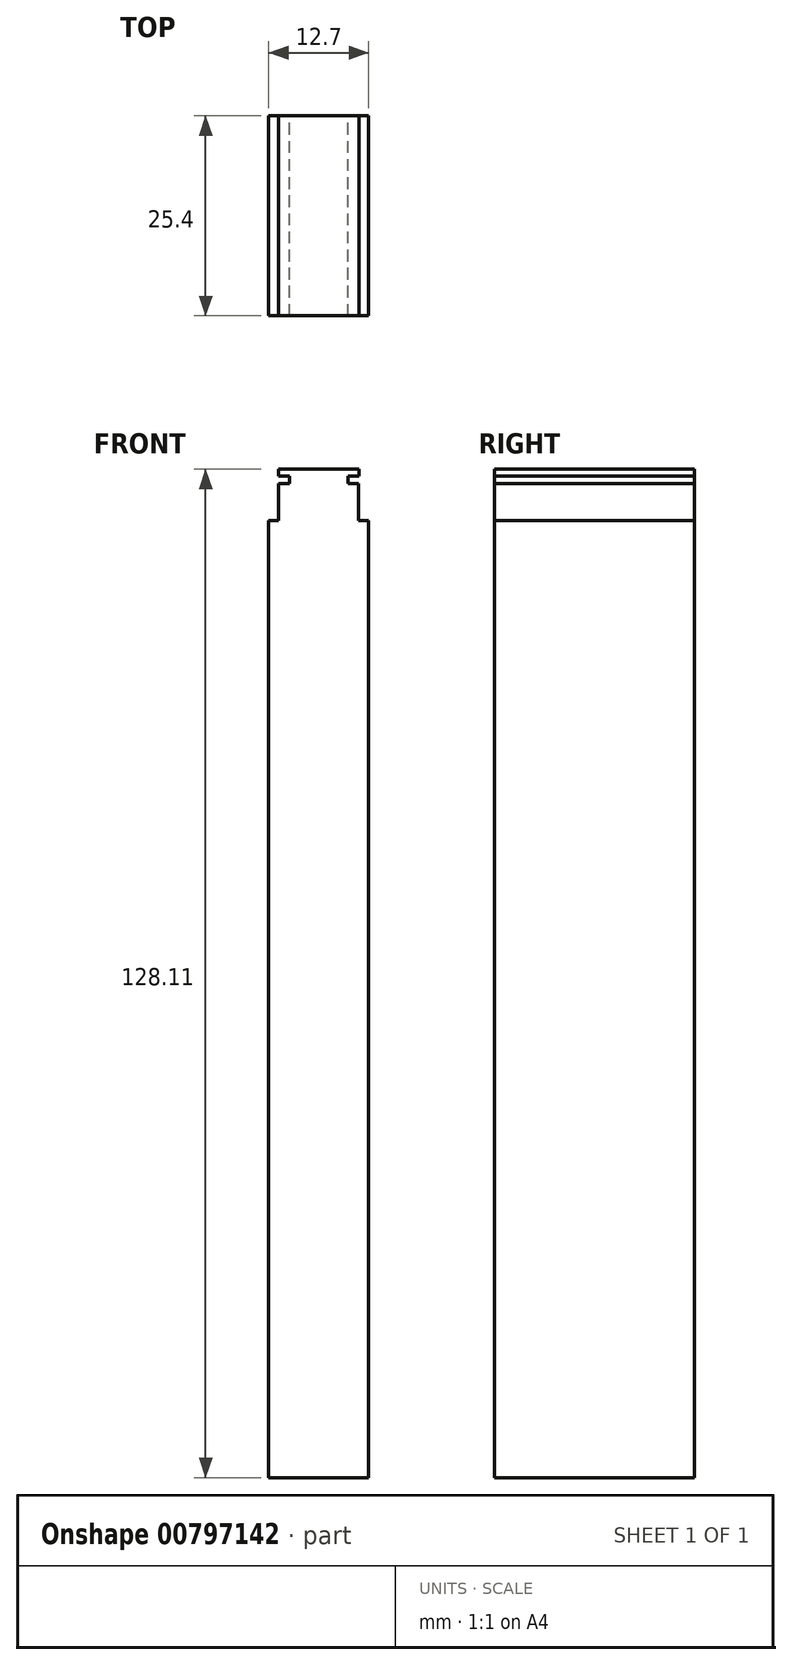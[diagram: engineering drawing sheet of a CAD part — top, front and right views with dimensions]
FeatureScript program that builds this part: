
annotation { "Feature Type Name" : "Feature", "Feature Type Description" : "" }
export const myFeature = defineFeature(function(context is Context, id is Id, definition is map)
    precondition{}
    {
        {
            var Q0;
            Q0=qCreatedBy(makeId("Front.planeOp"),FACE);
            var sketch = newSketch(context, id + "F0", { "sketchPlane" : qUnion([Q0])});
            skLineSegment(sketch, "E0.bottom", {"start": v(-6.35, 60.8) * mm, "end": v(6.35, 60.8) * mm});
            skLineSegment(sketch, "E0.top", {"start": v(-6.35, -60.8) * mm, "end": v(6.35, -60.8) * mm});
            skLineSegment(sketch, "E0.left", {"start": v(-6.35, 60.8) * mm, "end": v(-6.35, -60.8) * mm});
            skLineSegment(sketch, "E0.right", {"start": v(6.35, 60.8) * mm, "end": v(6.35, -60.8) * mm});
            skPoint(sketch, "E0.middle", {"position": v(0, 0) * mm});
            skLineSegment(sketch, "E1", {"start": v(0, 60.8) * mm, "end": v(0, -60.8) * mm});
            skLineSegment(sketch, "E2.bottom", {"start": v(-5.08, 60.8) * mm, "end": v(5.08, 60.8) * mm});
            skLineSegment(sketch, "E2.top", {"start": v(-5.08, 65.5) * mm, "end": v(5.08, 65.5) * mm});
            skLineSegment(sketch, "E2.left", {"start": v(-5.08, 60.8) * mm, "end": v(-5.08, 65.5) * mm});
            skLineSegment(sketch, "E2.right", {"start": v(5.08, 60.8) * mm, "end": v(5.08, 65.5) * mm});
            skLineSegment(sketch, "E3.bottom", {"start": v(-3.69, 65.5) * mm, "end": v(3.69, 65.5) * mm});
            skLineSegment(sketch, "E3.top", {"start": v(-3.69, 66.45) * mm, "end": v(3.69, 66.45) * mm});
            skLineSegment(sketch, "E3.left", {"start": v(-3.69, 65.5) * mm, "end": v(-3.69, 66.45) * mm});
            skLineSegment(sketch, "E3.right", {"start": v(3.69, 65.5) * mm, "end": v(3.69, 66.45) * mm});
            skLineSegment(sketch, "E4.bottom", {"start": v(-5.08, 66.45) * mm, "end": v(5.1, 66.45) * mm});
            skLineSegment(sketch, "E4.top", {"start": v(-5.08, 67.3) * mm, "end": v(5.1, 67.3) * mm});
            skLineSegment(sketch, "E4.left", {"start": v(-5.08, 66.45) * mm, "end": v(-5.08, 67.3) * mm});
            skLineSegment(sketch, "E4.right", {"start": v(5.1, 66.45) * mm, "end": v(5.1, 67.3) * mm});
            skLineSegment(sketch, "E5", {"start": v(0, 67.3) * mm, "end": v(0, -60.8) * mm});
            skPoint(sketch, "E5.startSnap0", {"position": v(0, 66.45) * mm});
            skSolve(sketch);
        }
        {
            var Q0;
            {var subQ0=sQuery(id+"F0.wireOp",EDGE,"E4.left");var subQ5=sQuery(id+"F0.wireOp",EDGE,"E3.left");var subQ11=sQuery(id+"F0.wireOp",EDGE,"E2.left");var subQ22=sQuery(id+"F0.wireOp",EDGE,"E0.left");var subQ26=sQuery(id+"F0.wireOp",EDGE,"E3.right");var subQ32=sQuery(id+"F0.wireOp",EDGE,"E2.right");var subQ35=sQuery(id+"F0.wireOp",EDGE,"E0.right");var subQ36=sQuery(id+"F0.wireOp",EDGE,"E4.right");Q0=qUnion([makeQuery(id+"F0.imprint","IMPRINT",FACE,{"disambiguationData":[TD([[makeQuery(id+"F0.imprint","IMPRINT",EDGE,{"derivedFrom":subQ36}),1.0]])]}),makeQuery(id+"F0.imprint","IMPRINT",FACE,{"disambiguationData":[TD([[makeQuery(id+"F0.imprint","IMPRINT",EDGE,{"derivedFrom":subQ5}),-1.0]])]}),makeQuery(id+"F0.imprint","IMPRINT",FACE,{"disambiguationData":[TD([[makeQuery(id+"F0.imprint","IMPRINT",EDGE,{"derivedFrom":subQ35}),-1.0]])]}),makeQuery(id+"F0.imprint","IMPRINT",FACE,{"disambiguationData":[TD([[makeQuery(id+"F0.imprint","IMPRINT",EDGE,{"derivedFrom":subQ32}),1.0]])]}),makeQuery(id+"F0.imprint","IMPRINT",FACE,{"disambiguationData":[TD([[makeQuery(id+"F0.imprint","IMPRINT",EDGE,{"derivedFrom":subQ26}),1.0]])]}),makeQuery(id+"F0.imprint","IMPRINT",FACE,{"disambiguationData":[TD([[makeQuery(id+"F0.imprint","IMPRINT",EDGE,{"derivedFrom":subQ22}),1.0]])]}),makeQuery(id+"F0.imprint","IMPRINT",FACE,{"disambiguationData":[TD([[makeQuery(id+"F0.imprint","IMPRINT",EDGE,{"derivedFrom":subQ11}),-1.0]])]}),makeQuery(id+"F0.imprint","IMPRINT",FACE,{"disambiguationData":[TD([[makeQuery(id+"F0.imprint","IMPRINT",EDGE,{"derivedFrom":subQ0}),-1.0]])]})]);}
            extrude(context, id + "F1", {"entities" : qUnion([Q0]), "depth" : 25.4 * mm, "offsetDistance" : 25.4 * mm});
        }
    });
